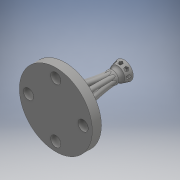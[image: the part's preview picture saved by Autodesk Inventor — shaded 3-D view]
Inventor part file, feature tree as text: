
AUTODESK INVENTOR PART (.ipt)
format: ipt  version: 2017 (Build 210142000, 142)  size: 649,216 bytes
history: native  units: mm
features: sketch x12, plane x7, extrude x4, pattern_circular x4, revolve x3, hole x1, sweep x1
ambient origin geometry x8: Origin, YZ Plane, XZ Plane, XY Plane, X Axis, Y Axis, Z Axis, Center Point
bodies: Solid1 (feature_tree)
feature tree (32):
  revolve  "Revolution1"  [1 undecoded]
  hole  "Hole1"  [1 undecoded]
  extrude  "Extrusion1"  Depth=4.0mm
  revolve  "Revolution2"  [1 undecoded]
  sketch  "Sketch5"  dims[d8=12.0mm d9=90.0deg]
  plane  "Work Plane1"
  sketch  "Sketch6"  dims[d10=12.0mm]
  plane  "Work Plane2"
  sweep  "Sweep2"
  pattern_circular  "Circular Pattern2"  Angle=90.0deg  [1 undecoded]
  plane  "Work Plane4"
  extrude  "Extrusion3"  Depth=8.0mm
  pattern_circular  "Circular Pattern3"  [2 undecoded]
  plane  "Work Plane6"
  extrude  "Extrusion4"  Depth=8.0mm
  pattern_circular  "Circular Pattern4"  [2 undecoded]
  plane  "Work Plane7"
  extrude  "Extrusion5"  Depth=2.0mm
  pattern_circular  "Circular Pattern5"  [2 undecoded]
  revolve  "Revolution3"  Angle=360.0deg
  sketch  "Sketch1"  dims[d0=16.0mm d1=4.0mm]
  sketch  "Sketch2"  dims[d2=90.0deg d3=8.0mm]
  sketch  "Sketch3"  dims[d4=30.0mm d5=4.0mm]
  sketch  "Sketch4"  dims[d6=90.0deg d7=12.0mm]
  sketch  "Sketch8"  dims[d11=12.0mm]
  sketch  "Sketch9"  dims[d12=12.0mm]
  plane  "Work Plane3"
  sketch  "Sketch10"  dims[d13=90.0deg]
  plane  "Work Plane5"
  sketch  "Sketch11"  dims[d14=4.5mm d15=6.0mm d16=4.0mm d17=2.0mm d18=90.0deg d19=8.0mm d20=20.594885mm]
  sketch  "Sketch12"  dims[d21=28.75mm d22=0.0mm]
  sketch  "Sketch13"  dims[d23=45.0mm d24=90.0deg d25=8.0mm d26=1.745329mm d27=8.0mm d32=-1.5mm d39=2.0mm d40=0.0mm d41=0.0mm d42=80.0mm d43=360.0deg d45=19.024089mm d46=-5.2mm d47=3.0mm d48=0.0mm d49=80.0mm d50=360.0deg d52=17.453293mm d53=-4.5mm d54=3.0mm d55=0.0mm d56=40.0mm d57=360.0deg d59=3.25mm d60=2.0mm d61=0.0mm d62=80.0mm d63=360.0deg d65=90.0deg]
note: 10 required parameter values undecoded (feature->parameter linkage not recoverable at this tier; creation-order binding heuristic only, values carry confidence <= 0.55)